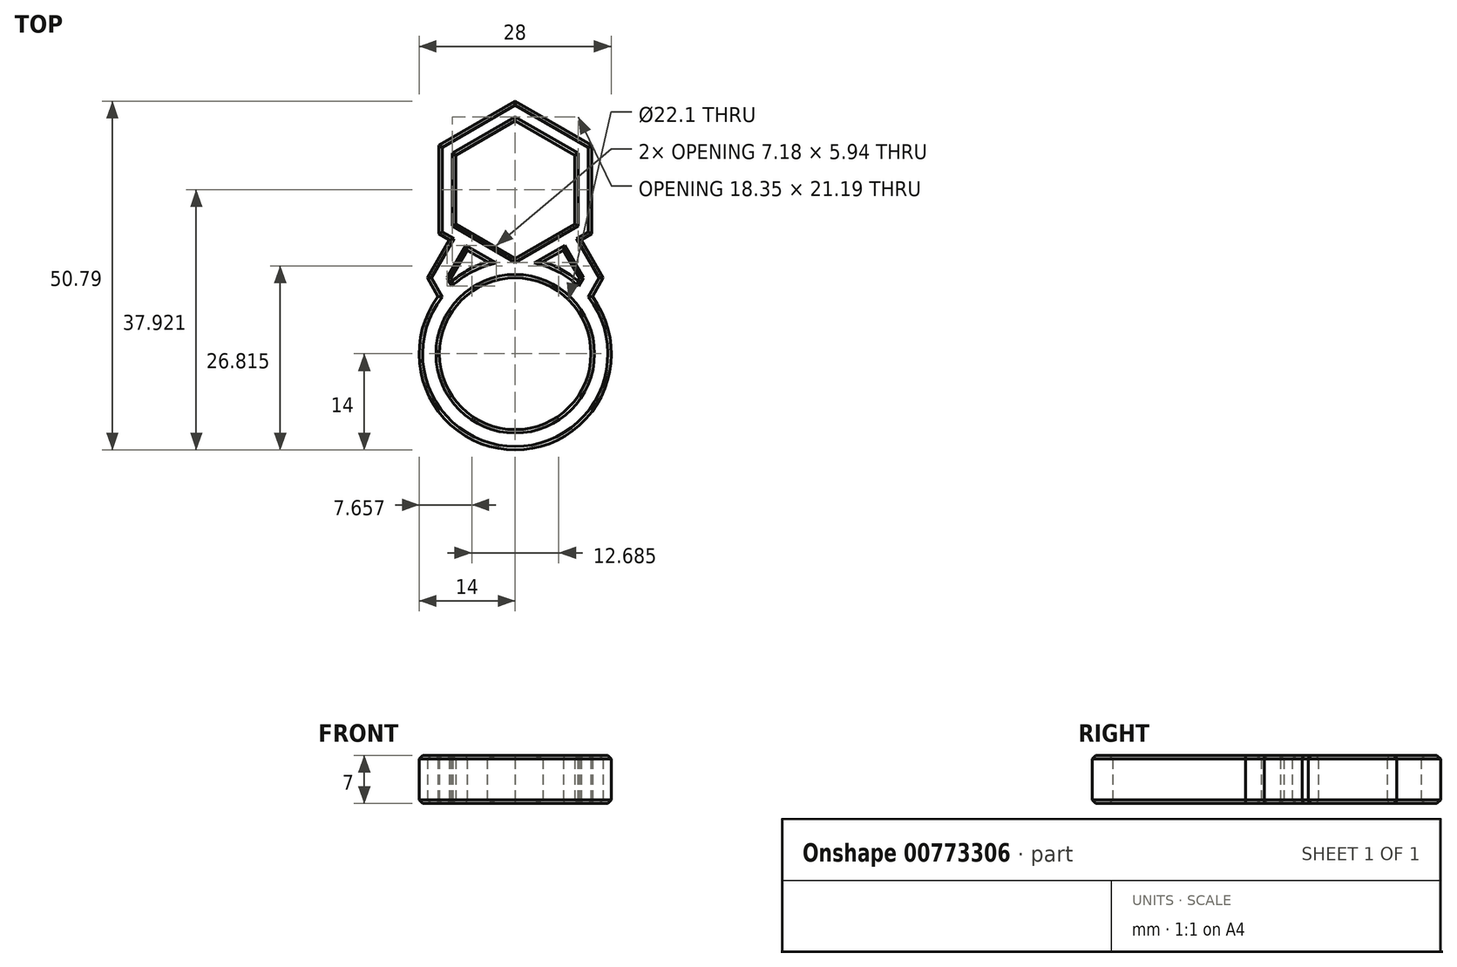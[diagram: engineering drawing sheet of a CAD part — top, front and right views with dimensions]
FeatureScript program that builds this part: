
annotation { "Feature Type Name" : "Feature", "Feature Type Description" : "" }
export const myFeature = defineFeature(function(context is Context, id is Id, definition is map)
    precondition{}
    {
        {
            var Q0;
            Q0=qCreatedBy(makeId("Top.planeOp"),FACE);
            var sketch = newSketch(context, id + "F0", { "sketchPlane" : qUnion([Q0])});
            skCircle(sketch, "E0", {"center": v(0, 0) * mm, "radius": 11.05 * mm});
            skCircle(sketch, "E1.cCircle", {"center": v(0, 23.92) * mm, "radius": 10.02 * mm, "construction": true});
            skLineSegment(sketch, "E1.0", {"start": v(0, 33.94) * mm, "end": v(8.68, 28.93) * mm});
            skLineSegment(sketch, "E1.1", {"start": v(8.67, 28.93) * mm, "end": v(8.68, 18.91) * mm});
            skLineSegment(sketch, "E1.2", {"start": v(8.67, 18.91) * mm, "end": v(0, 13.9) * mm});
            skLineSegment(sketch, "E1.3", {"start": v(0, 13.9) * mm, "end": v(-8.67, 18.91) * mm});
            skLineSegment(sketch, "E1.4", {"start": v(-8.67, 18.91) * mm, "end": v(-8.68, 28.93) * mm});
            skLineSegment(sketch, "E1.5", {"start": v(-8.67, 28.93) * mm, "end": v(0, 33.94) * mm});
            skCircle(sketch, "E2.cCircle", {"center": v(0, 11.05) * mm, "radius": 9.36 * mm, "construction": true});
            skLineSegment(sketch, "E2.0", {"start": v(9.36, 11.05) * mm, "end": v(4.68, 2.95) * mm});
            skLineSegment(sketch, "E2.1", {"start": v(4.68, 2.95) * mm, "end": v(-4.68, 2.95) * mm});
            skLineSegment(sketch, "E2.2", {"start": v(-4.68, 2.95) * mm, "end": v(-9.36, 11.05) * mm});
            skLineSegment(sketch, "E2.3", {"start": v(-9.36, 11.05) * mm, "end": v(-4.68, 19.15) * mm});
            skLineSegment(sketch, "E2.4", {"start": v(-4.68, 19.15) * mm, "end": v(4.68, 19.15) * mm});
            skLineSegment(sketch, "E2.5", {"start": v(4.68, 19.15) * mm, "end": v(9.36, 11.05) * mm});
            skLineSegment(sketch, "E3", {"start": v(0, 11.05) * mm, "end": v(30.07, 11.05) * mm, "construction": true});
            skLineSegment(sketch, "E4.0", {"start": v(-6.4, -0.05) * mm, "end": v(-12.82, 11.05) * mm});
            skLineSegment(sketch, "E4.1", {"start": v(-6.4, 22.15) * mm, "end": v(6.4, 22.15) * mm});
            skLineSegment(sketch, "E4.2", {"start": v(6.4, 22.15) * mm, "end": v(12.82, 11.05) * mm});
            skLineSegment(sketch, "E4.3", {"start": v(-12.82, 11.05) * mm, "end": v(-6.4, 22.15) * mm});
            skLineSegment(sketch, "E4.4", {"start": v(12.82, 11.05) * mm, "end": v(6.4, -0.05) * mm});
            skLineSegment(sketch, "E4.5", {"start": v(6.4, -0.05) * mm, "end": v(-6.4, -0.05) * mm});
            skCircle(sketch, "E5", {"center": v(0, 0) * mm, "radius": 14 * mm});
            skCircle(sketch, "E6.cCircle", {"center": v(0, 23.92) * mm, "radius": 12.87 * mm, "construction": true});
            skLineSegment(sketch, "E6.0", {"start": v(0, 11.05) * mm, "end": v(-11.15, 17.49) * mm});
            skLineSegment(sketch, "E6.1", {"start": v(-11.15, 17.49) * mm, "end": v(-11.15, 30.36) * mm});
            skLineSegment(sketch, "E6.2", {"start": v(-11.15, 30.36) * mm, "end": v(0, 36.8) * mm});
            skLineSegment(sketch, "E6.3", {"start": v(0, 36.8) * mm, "end": v(11.15, 30.36) * mm});
            skLineSegment(sketch, "E6.4", {"start": v(11.15, 30.36) * mm, "end": v(11.15, 17.49) * mm});
            skLineSegment(sketch, "E6.5", {"start": v(11.15, 17.49) * mm, "end": v(0, 11.05) * mm});
            skSolve(sketch);
        }
        {
            var Q0;
            {var subQ5=sQuery(id+"F0.wireOp",EDGE,"E1.0");Q0=makeQuery(id+"F0.imprint","IMPRINT",FACE,{"disambiguationData":[TD([[makeQuery(id+"F0.imprint","IMPRINT",EDGE,{"derivedFrom":subQ5}),1.0]])]});}
            var Q1;
            {var subQ1=sQuery(id+"F0.wireOp",EDGE,"E1.3");var subQ5=sQuery(id+"F0.wireOp",EDGE,"E1.4");var subQ6=makeQuery(id+"F0.imprint","INTERSECT",VERTEX,{"derivedFrom":[subQ1,subQ5]});Q1=makeQuery(id+"F0.imprint","IMPRINT",FACE,{"disambiguationData":[TD([[makeQuery(id+"F0.imprint","IMPRINT",EDGE,{"disambiguationData":[TD([[subQ6,1.0]])],"derivedFrom":subQ1}),1.0]])]});}
            var Q2;
            {var subQ1=sQuery(id+"F0.wireOp",EDGE,"E1.2");var subQ6=sQuery(id+"F0.wireOp",EDGE,"E1.3");var subQ13=makeQuery(id+"F0.imprint","INTERSECT",VERTEX,{"derivedFrom":[subQ1,subQ6]});Q2=makeQuery(id+"F0.imprint","IMPRINT",FACE,{"disambiguationData":[TD([[makeQuery(id+"F0.imprint","IMPRINT",EDGE,{"disambiguationData":[TD([[subQ13,1.0]])],"derivedFrom":subQ1}),1.0]])]});}
            var Q3;
            {var subQ3=sQuery(id+"F0.wireOp",EDGE,"E1.1");var subQ5=sQuery(id+"F0.wireOp",EDGE,"E1.2");var subQ6=makeQuery(id+"F0.imprint","INTERSECT",VERTEX,{"derivedFrom":[subQ3,subQ5]});Q3=makeQuery(id+"F0.imprint","IMPRINT",FACE,{"disambiguationData":[TD([[makeQuery(id+"F0.imprint","IMPRINT",EDGE,{"disambiguationData":[TD([[subQ6,1.0]])],"derivedFrom":subQ3}),1.0]])]});}
            var Q4;
            {var subQ5=sQuery(id+"F0.wireOp",EDGE,"E2.5");var subQ6=sQuery(id+"F0.wireOp",EDGE,"E2.0");var subQ7=makeQuery(id+"F0.imprint","INTERSECT",VERTEX,{"derivedFrom":[subQ6,subQ5]});Q4=makeQuery(id+"F0.imprint","IMPRINT",FACE,{"disambiguationData":[TD([[makeQuery(id+"F0.imprint","IMPRINT",EDGE,{"disambiguationData":[TD([[subQ7,-1.0]])],"derivedFrom":subQ6}),1.0]])]});}
            var Q5;
            {var subQ0=sQuery(id+"F0.wireOp",EDGE,"E2.0");var subQ1=sQuery(id+"F0.wireOp",EDGE,"E0");var subQ2=makeQuery(id+"F0.imprint","INTERSECT",VERTEX,{"derivedFrom":[subQ1,subQ0]});Q5=makeQuery(id+"F0.imprint","IMPRINT",FACE,{"disambiguationData":[TD([[makeQuery(id+"F0.imprint","IMPRINT",EDGE,{"disambiguationData":[TD([[subQ2,1.0]])],"derivedFrom":subQ1}),-1.0]])]});}
            var Q6;
            {var subQ1=sQuery(id+"F0.wireOp",EDGE,"E0");var subQ3=sQuery(id+"F0.wireOp",EDGE,"E2.0");var subQ4=makeQuery(id+"F0.imprint","INTERSECT",VERTEX,{"derivedFrom":[subQ1,subQ3]});Q6=makeQuery(id+"F0.imprint","IMPRINT",FACE,{"disambiguationData":[TD([[makeQuery(id+"F0.imprint","IMPRINT",EDGE,{"disambiguationData":[TD([[subQ4,1.0]])],"derivedFrom":subQ3}),-1.0]])]});}
            var Q7;
            {var subQ1=sQuery(id+"F0.wireOp",EDGE,"E0");var subQ3=sQuery(id+"F0.wireOp",EDGE,"E2.2");var subQ4=makeQuery(id+"F0.imprint","INTERSECT",VERTEX,{"derivedFrom":[subQ1,subQ3]});Q7=makeQuery(id+"F0.imprint","IMPRINT",FACE,{"disambiguationData":[TD([[makeQuery(id+"F0.imprint","IMPRINT",EDGE,{"disambiguationData":[TD([[subQ4,-1.0]])],"derivedFrom":subQ3}),-1.0]])]});}
            var Q8;
            {var subQ0=sQuery(id+"F0.wireOp",EDGE,"E6.5");var subQ1=sQuery(id+"F0.wireOp",EDGE,"E5");var subQ2=makeQuery(id+"F0.imprint","INTERSECT",VERTEX,{"derivedFrom":[subQ1,subQ0]});Q8=makeQuery(id+"F0.imprint","IMPRINT",FACE,{"disambiguationData":[TD([[makeQuery(id+"F0.imprint","IMPRINT",EDGE,{"disambiguationData":[TD([[subQ2,-1.0]])],"derivedFrom":subQ1}),1.0]])]});}
            var Q9;
            {var subQ0=sQuery(id+"F0.wireOp",EDGE,"E4.4");var subQ1=sQuery(id+"F0.wireOp",EDGE,"E0");var subQ2=makeQuery(id+"F0.imprint","INTERSECT",VERTEX,{"derivedFrom":[subQ1,subQ0]});Q9=makeQuery(id+"F0.imprint","IMPRINT",FACE,{"disambiguationData":[TD([[makeQuery(id+"F0.imprint","IMPRINT",EDGE,{"disambiguationData":[TD([[subQ2,1.0]])],"derivedFrom":subQ1}),-1.0]])]});}
            var Q10;
            {var subQ0=sQuery(id+"F0.wireOp",EDGE,"E2.2");var subQ1=sQuery(id+"F0.wireOp",EDGE,"E0");var subQ2=makeQuery(id+"F0.imprint","INTERSECT",VERTEX,{"derivedFrom":[subQ1,subQ0]});Q10=makeQuery(id+"F0.imprint","IMPRINT",FACE,{"disambiguationData":[TD([[makeQuery(id+"F0.imprint","IMPRINT",EDGE,{"disambiguationData":[TD([[subQ2,-1.0]])],"derivedFrom":subQ1}),-1.0]])]});}
            var Q11;
            {var subQ0=sQuery(id+"F0.wireOp",EDGE,"E2.3");var subQ1=sQuery(id+"F0.wireOp",EDGE,"E2.2");var subQ2=makeQuery(id+"F0.imprint","INTERSECT",VERTEX,{"derivedFrom":[subQ1,subQ0]});Q11=makeQuery(id+"F0.imprint","IMPRINT",FACE,{"disambiguationData":[TD([[makeQuery(id+"F0.imprint","IMPRINT",EDGE,{"disambiguationData":[TD([[subQ2,1.0]])],"derivedFrom":subQ1}),1.0]])]});}
            var Q12;
            {var subQ0=sQuery(id+"F0.wireOp",EDGE,"E5");var subQ1=sQuery(id+"F0.wireOp",EDGE,"E1.3");var subQ2=makeQuery(id+"F0.imprint","INTERSECT",VERTEX,{"derivedFrom":[subQ1,subQ0]});Q12=makeQuery(id+"F0.imprint","IMPRINT",FACE,{"disambiguationData":[TD([[makeQuery(id+"F0.imprint","IMPRINT",EDGE,{"disambiguationData":[TD([[subQ2,-1.0]])],"derivedFrom":subQ1}),1.0]])]});}
            var Q13;
            {var subQ0=sQuery(id+"F0.wireOp",EDGE,"E2.3");var subQ1=sQuery(id+"F0.wireOp",EDGE,"E1.3");var subQ2=makeQuery(id+"F0.imprint","INTERSECT",VERTEX,{"derivedFrom":[subQ1,subQ0]});Q13=makeQuery(id+"F0.imprint","IMPRINT",FACE,{"disambiguationData":[TD([[makeQuery(id+"F0.imprint","IMPRINT",EDGE,{"disambiguationData":[TD([[subQ2,-1.0]])],"derivedFrom":subQ1}),1.0]])]});}
            var Q14;
            {var subQ0=sQuery(id+"F0.wireOp",EDGE,"E4.2");var subQ1=sQuery(id+"F0.wireOp",EDGE,"E1.2");var subQ2=makeQuery(id+"F0.imprint","INTERSECT",VERTEX,{"derivedFrom":[subQ1,subQ0]});Q14=makeQuery(id+"F0.imprint","IMPRINT",FACE,{"disambiguationData":[TD([[makeQuery(id+"F0.imprint","IMPRINT",EDGE,{"disambiguationData":[TD([[subQ2,-1.0]])],"derivedFrom":subQ1}),1.0]])]});}
            var Q15;
            {var subQ0=sQuery(id+"F0.wireOp",EDGE,"E2.5");var subQ1=sQuery(id+"F0.wireOp",EDGE,"E1.2");var subQ2=makeQuery(id+"F0.imprint","INTERSECT",VERTEX,{"derivedFrom":[subQ1,subQ0]});Q15=makeQuery(id+"F0.imprint","IMPRINT",FACE,{"disambiguationData":[TD([[makeQuery(id+"F0.imprint","IMPRINT",EDGE,{"disambiguationData":[TD([[subQ2,-1.0]])],"derivedFrom":subQ1}),1.0]])]});}
            extrude(context, id + "F1", {"entities" : qUnion([Q0, Q1, Q2, Q3, Q4, Q5, Q6, Q7, Q8, Q9, Q10, Q11, Q12, Q13, Q14, Q15]), "depth" : 7 * mm, "offsetDistance" : 25 * mm});
        }
        {
            var Q0;
            Q0=makeQuery(id+"FxanIWPpTdxQHp1_1.opPattern","COPY",EDGE,{"derivedFrom":makeQuery(id+"F1.opExtrude","CAP_EDGE",EDGE,{"disambiguationData":[OSD([sQuery(id+"F0.wireOp",EDGE,"E6.1")])],"isStart":false}),"instanceName":"2"});
            var Q1;
            Q1=makeQuery(id+"FxanIWPpTdxQHp1_1.opPattern","COPY",EDGE,{"derivedFrom":makeQuery(id+"F1.opExtrude","CAP_EDGE",EDGE,{"disambiguationData":[OSD([sQuery(id+"F0.wireOp",EDGE,"E6.2")])],"isStart":false}),"instanceName":"2"});
            var Q2;
            Q2=makeQuery(id+"FxanIWPpTdxQHp1_1.opPattern","COPY",EDGE,{"derivedFrom":makeQuery(id+"F1.opExtrude","CAP_EDGE",EDGE,{"disambiguationData":[OSD([sQuery(id+"F0.wireOp",EDGE,"E6.3")])],"isStart":false}),"instanceName":"2"});
            var Q3;
            Q3=makeQuery(id+"FxanIWPpTdxQHp1_1.opPattern","COPY",EDGE,{"derivedFrom":makeQuery(id+"F1.opExtrude","CAP_EDGE",EDGE,{"disambiguationData":[OSD([sQuery(id+"F0.wireOp",EDGE,"E6.4")])],"isStart":false}),"instanceName":"2"});
            var Q4;
            {var subQ0=sQuery(id+"F0.wireOp",EDGE,"E6.5");Q4=makeQuery(id+"FxanIWPpTdxQHp1_1.opPattern","COPY",EDGE,{"derivedFrom":makeQuery(id+"F1.opExtrude","CAP_EDGE",EDGE,{"disambiguationData":[OSD([subQ0]),TDD([makeQuery(id+"F0.imprint","IMPRINT",EDGE,{"disambiguationData":[TD([[makeQuery(id+"F0.imprint","INTERSECT",VERTEX,{"derivedFrom":[sQuery(id+"F0.wireOp",EDGE,"E6.4"),subQ0]}),-1.0]])],"derivedFrom":subQ0})])],"isStart":false}),"instanceName":"2"});}
            var Q5;
            Q5=makeQuery(id+"FxanIWPpTdxQHp1_1.opPattern","COPY",EDGE,{"derivedFrom":makeQuery(id+"F1.opExtrude","CAP_EDGE",EDGE,{"disambiguationData":[OSD([sQuery(id+"F0.wireOp",EDGE,"E4.2")])],"isStart":false}),"instanceName":"2"});
            var Q6;
            Q6=makeQuery(id+"FxanIWPpTdxQHp1_1.opPattern","COPY",EDGE,{"derivedFrom":makeQuery(id+"F1.opExtrude","CAP_EDGE",EDGE,{"disambiguationData":[OSD([sQuery(id+"F0.wireOp",EDGE,"E4.4")])],"isStart":false}),"instanceName":"2"});
            var Q7;
            {var subQ0=sQuery(id+"F0.wireOp",EDGE,"E4.0");var subQ1=sQuery(id+"F0.wireOp",EDGE,"E5");var subQ4=makeQuery(id+"F0.imprint","IMPRINT",EDGE,{"disambiguationData":[TD([[makeQuery(id+"F0.imprint","INTERSECT",VERTEX,{"derivedFrom":[subQ0,subQ1]}),-1.0]])],"derivedFrom":subQ1});Q7=makeQuery(id+"FxanIWPpTdxQHp1_1.boolean.opBoolean","SPLIT",EDGE,{"disambiguationData":[TD([makeQuery(id+"FxanIWPpTdxQHp1_1.opPattern","COPY",FACE,{"derivedFrom":makeQuery(id+"F1.opExtrude","SWEPT_FACE",FACE,{"disambiguationData":[OSD([subQ0])]}),"instanceName":"1"})])],"derivedFrom":makeQuery(id+"F1.opExtrude","CAP_EDGE",EDGE,{"disambiguationData":[OSD([subQ1]),TDD([subQ4])],"isStart":false})});}
            var Q8;
            Q8=makeQuery(id+"FxanIWPpTdxQHp1_1.opPattern","COPY",EDGE,{"derivedFrom":makeQuery(id+"F1.opExtrude","CAP_EDGE",EDGE,{"disambiguationData":[OSD([sQuery(id+"F0.wireOp",EDGE,"E4.0")])],"isStart":false}),"instanceName":"1"});
            var Q9;
            Q9=makeQuery(id+"FxanIWPpTdxQHp1_1.opPattern","COPY",EDGE,{"derivedFrom":makeQuery(id+"F1.opExtrude","CAP_EDGE",EDGE,{"disambiguationData":[OSD([sQuery(id+"F0.wireOp",EDGE,"E4.3")])],"isStart":false}),"instanceName":"1"});
            var Q10;
            {var subQ0=makeQuery(id+"F1.opExtrude","CAP_FACE",FACE,{"disambiguationData":[OSD([sQuery(id+"F0.wireOp",EDGE,"E0"),sQuery(id+"F0.wireOp",EDGE,"E1.0"),sQuery(id+"F0.wireOp",EDGE,"E1.1"),sQuery(id+"F0.wireOp",EDGE,"E1.2"),sQuery(id+"F0.wireOp",EDGE,"E1.3"),sQuery(id+"F0.wireOp",EDGE,"E1.4"),sQuery(id+"F0.wireOp",EDGE,"E1.5"),sQuery(id+"F0.wireOp",EDGE,"E2.0"),sQuery(id+"F0.wireOp",EDGE,"E2.2"),sQuery(id+"F0.wireOp",EDGE,"E2.3"),sQuery(id+"F0.wireOp",EDGE,"E2.5"),sQuery(id+"F0.wireOp",EDGE,"E4.0"),sQuery(id+"F0.wireOp",EDGE,"E4.2"),sQuery(id+"F0.wireOp",EDGE,"E4.3"),sQuery(id+"F0.wireOp",EDGE,"E4.4"),sQuery(id+"F0.wireOp",EDGE,"E5"),sQuery(id+"F0.wireOp",EDGE,"E6.0"),sQuery(id+"F0.wireOp",EDGE,"E6.1"),sQuery(id+"F0.wireOp",EDGE,"E6.2"),sQuery(id+"F0.wireOp",EDGE,"E6.3"),sQuery(id+"F0.wireOp",EDGE,"E6.4"),sQuery(id+"F0.wireOp",EDGE,"E6.5")])],"isStart":false});Q10=makeQuery(id+"FxanIWPpTdxQHp1_1.boolean.opBoolean","MERGE",FACE,{"derivedFrom":[subQ0,makeQuery(id+"FxanIWPpTdxQHp1_1.opPattern","COPY",FACE,{"derivedFrom":subQ0,"instanceName":"1"}),makeQuery(id+"FxanIWPpTdxQHp1_1.opPattern","COPY",FACE,{"derivedFrom":subQ0,"instanceName":"2"})]});}
            var Q11;
            {var subQ0=makeQuery(id+"F1.opExtrude","CAP_FACE",FACE,{"disambiguationData":[OSD([sQuery(id+"F0.wireOp",EDGE,"E0"),sQuery(id+"F0.wireOp",EDGE,"E1.0"),sQuery(id+"F0.wireOp",EDGE,"E1.1"),sQuery(id+"F0.wireOp",EDGE,"E1.2"),sQuery(id+"F0.wireOp",EDGE,"E1.3"),sQuery(id+"F0.wireOp",EDGE,"E1.4"),sQuery(id+"F0.wireOp",EDGE,"E1.5"),sQuery(id+"F0.wireOp",EDGE,"E2.0"),sQuery(id+"F0.wireOp",EDGE,"E2.2"),sQuery(id+"F0.wireOp",EDGE,"E2.3"),sQuery(id+"F0.wireOp",EDGE,"E2.5"),sQuery(id+"F0.wireOp",EDGE,"E4.0"),sQuery(id+"F0.wireOp",EDGE,"E4.2"),sQuery(id+"F0.wireOp",EDGE,"E4.3"),sQuery(id+"F0.wireOp",EDGE,"E4.4"),sQuery(id+"F0.wireOp",EDGE,"E5"),sQuery(id+"F0.wireOp",EDGE,"E6.0"),sQuery(id+"F0.wireOp",EDGE,"E6.1"),sQuery(id+"F0.wireOp",EDGE,"E6.2"),sQuery(id+"F0.wireOp",EDGE,"E6.3"),sQuery(id+"F0.wireOp",EDGE,"E6.4"),sQuery(id+"F0.wireOp",EDGE,"E6.5")])],"isStart":true});Q11=makeQuery(id+"FxanIWPpTdxQHp1_1.boolean.opBoolean","MERGE",FACE,{"derivedFrom":[subQ0,makeQuery(id+"FxanIWPpTdxQHp1_1.opPattern","COPY",FACE,{"derivedFrom":subQ0,"instanceName":"1"}),makeQuery(id+"FxanIWPpTdxQHp1_1.opPattern","COPY",FACE,{"derivedFrom":subQ0,"instanceName":"2"})]});}
            chamfer(context, id + "F2", {"entities" : qUnion([Q0, Q1, Q2, Q3, Q4, Q5, Q6, Q7, Q8, Q9, Q10, Q11]), "width" : .5 * mm, "tangentPropagation" : true});
        }
    });
